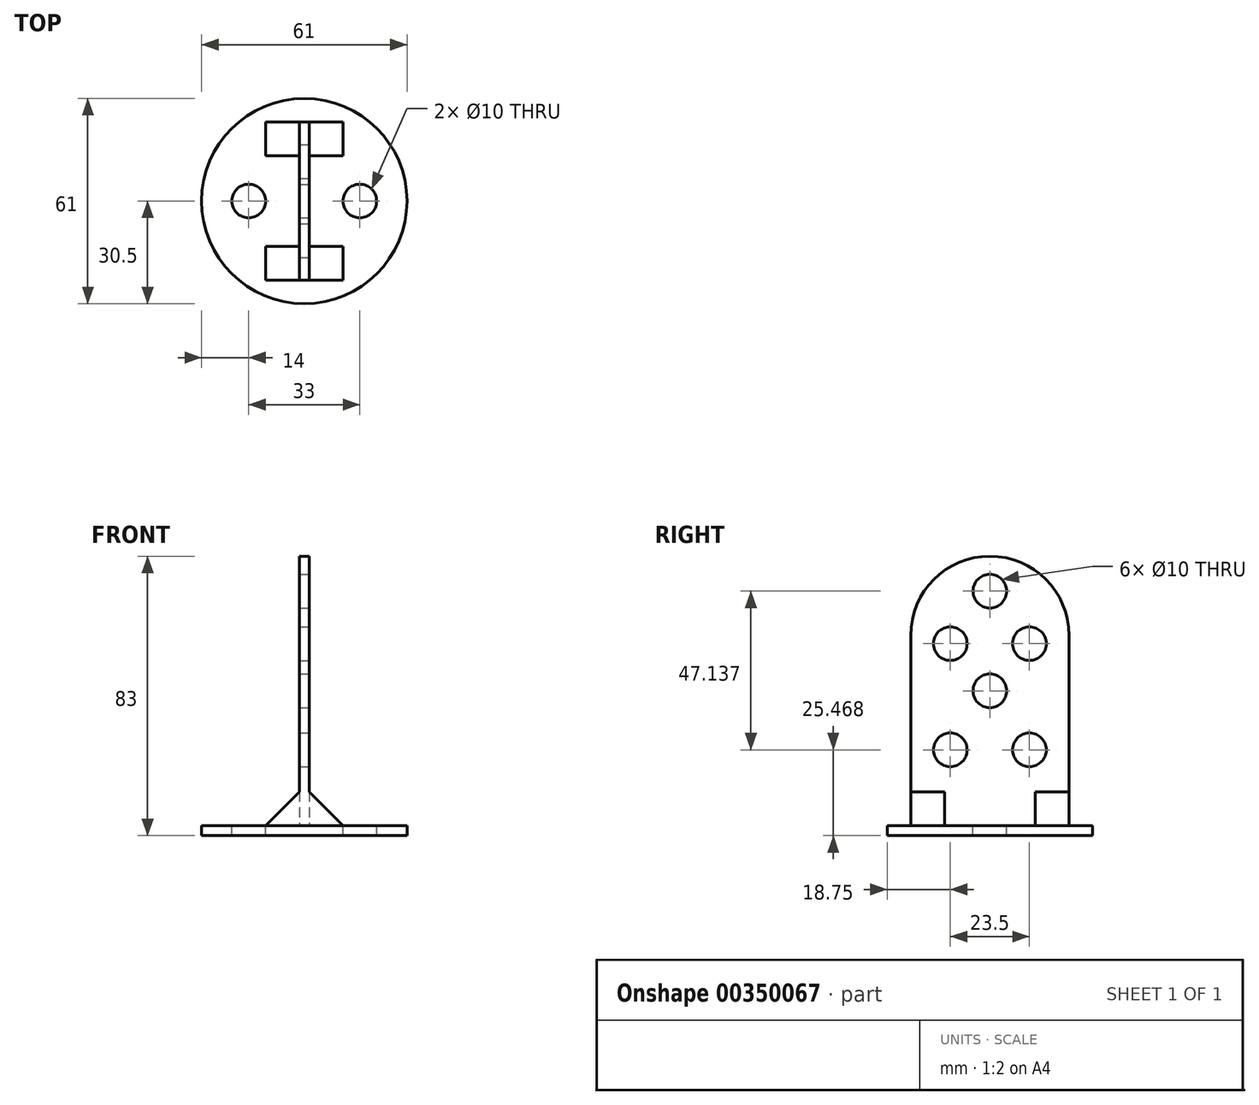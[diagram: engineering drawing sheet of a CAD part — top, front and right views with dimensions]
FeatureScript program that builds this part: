
annotation { "Feature Type Name" : "Feature", "Feature Type Description" : "" }
export const myFeature = defineFeature(function(context is Context, id is Id, definition is map)
    precondition{}
    {
        {
            var Q0;
            Q0=qCreatedBy(makeId("Top.planeOp"),FACE);
            var sketch = newSketch(context, id + "F0", { "sketchPlane" : qUnion([Q0])});
            skCircle(sketch, "E0", {"center": v(0, 0) * mm, "radius": 30.5 * mm});
            skSolve(sketch);
        }
        {
            var Q0;
            Q0=makeQuery(id+"F0.imprint","IMPRINT",FACE,{"disambiguationData":[TD([[makeQuery(id+"F0.imprint","IMPRINT",EDGE,{"derivedFrom":sQuery(id+"F0.wireOp",EDGE,"E0")}),1.0]])]});
            extrude(context, id + "F1", {"entities" : qUnion([Q0]), "depth" : 3 * mm});
        }
        {
            var Q0;
            Q0=makeQuery(id+"F1.opExtrude","CAP_FACE",FACE,{"disambiguationData":[OSD([sQuery(id+"F0.wireOp",EDGE,"E0")])],"isStart":false});
            var sketch = newSketch(context, id + "F2", { "sketchPlane" : qUnion([Q0])});
            skLineSegment(sketch, "E1", {"start": v(0, 56.72) * mm, "end": v(0, 23.5) * mm});
            skLineSegment(sketch, "E2", {"start": v(0, -59.64) * mm, "end": v(0, -23.5) * mm});
            skLineSegment(sketch, "E3", {"start": v(1.5, 0) * mm, "end": v(68.94, 0) * mm});
            skLineSegment(sketch, "E4", {"start": v(68.94, 0) * mm, "end": v(1.5, 0) * mm});
            skLineSegment(sketch, "E5.bottom", {"start": v(0, 23.5) * mm, "end": v(1.5, 23.5) * mm});
            skLineSegment(sketch, "E5.top", {"start": v(0, -23.5) * mm, "end": v(1.5, -23.5) * mm});
            skLineSegment(sketch, "E5.right", {"start": v(1.5, 23.5) * mm, "end": v(1.5, -23.5) * mm});
            skLineSegment(sketch, "E6.bottom", {"start": v(0, 23.5) * mm, "end": v(-1.5, 23.5) * mm});
            skLineSegment(sketch, "E6.top", {"start": v(0, -23.5) * mm, "end": v(-1.5, -23.5) * mm});
            skLineSegment(sketch, "E6.right", {"start": v(-1.5, 23.5) * mm, "end": v(-1.5, -23.5) * mm});
            skLineSegment(sketch, "E7.trimOffspring", {"start": v(0, -23.5) * mm, "end": v(0, -59.64) * mm});
            skLineSegment(sketch, "E8.trimOffspring", {"start": v(-1.5, 0) * mm, "end": v(-64.93, 0) * mm});
            skPoint(sketch, "E6.left.start.orphan", {"position": v(0, 0) * mm});
            skSolve(sketch);
        }
        {
            var Q0;
            {var subQ3=sQuery(id+"F2.wireOp",EDGE,"E5.bottom");Q0=makeQuery(id+"F2.imprint","IMPRINT",FACE,{"disambiguationData":[TD([[makeQuery(id+"F2.imprint","IMPRINT",EDGE,{"derivedFrom":subQ3}),-1.0]])]});}
            extrude(context, id + "F3", {"entities" : qUnion([Q0]), "operationType" : NewBodyOperationType.ADD, "depth" : 80 * mm});
        }
        {
            var Q0;
            Q0=makeQuery(id+"F3.opExtrude","CAP_EDGE",EDGE,{"disambiguationData":[OSD([sQuery(id+"F2.wireOp",EDGE,"E5.bottom"),sQuery(id+"F2.wireOp",EDGE,"E6.bottom")])],"isStart":false});
            var Q1;
            Q1=makeQuery(id+"F3.opExtrude","CAP_EDGE",EDGE,{"disambiguationData":[OSD([sQuery(id+"F2.wireOp",EDGE,"E5.top"),sQuery(id+"F2.wireOp",EDGE,"E6.top")])],"isStart":false});
            fillet(context, id + "F4", {"entities" : qUnion([Q0, Q1]), "radius" : 23.5 * mm, "tangentPropagation" : true, "allowEdgeOverflow" : false});
        }
        {
            var Q0;
            Q0=makeQuery(id+"F1.opExtrude","CAP_FACE",FACE,{"disambiguationData":[OSD([sQuery(id+"F0.wireOp",EDGE,"E0")])],"isStart":false});
            var sketch = newSketch(context, id + "F5", { "sketchPlane" : qUnion([Q0])});
            skLineSegment(sketch, "E9", {"start": v(1.5, -23.5) * mm, "end": v(1.5, -13.5) * mm});
            skLineSegment(sketch, "E10", {"start": v(1.5, -23.5) * mm, "end": v(11.5, -23.5) * mm});
            skLineSegment(sketch, "E11.top", {"start": v(1.5, -13.5) * mm, "end": v(11.5, -13.5) * mm});
            skLineSegment(sketch, "E11.right", {"start": v(11.5, -23.5) * mm, "end": v(11.5, -13.5) * mm});
            skSolve(sketch);
        }
        {
            var Q0;
            Q0=makeQuery(id+"F5.imprint","IMPRINT",FACE,{"disambiguationData":[TD([[makeQuery(id+"F5.imprint","IMPRINT",EDGE,{"derivedFrom":sQuery(id+"F5.wireOp",EDGE,"E10")}),1.0]])]});
            extrude(context, id + "F6", {"entities" : qUnion([Q0]), "operationType" : NewBodyOperationType.ADD, "depth" : 10 * mm});
        }
        {
            var Q0;
            Q0=makeQuery(id+"F6.opExtrude","CAP_EDGE",EDGE,{"disambiguationData":[OSD([sQuery(id+"F5.wireOp",EDGE,"E11.right")])],"isStart":false});
            chamfer(context, id + "F7", {"entities" : qUnion([Q0]), "width" : 10 * mm, "tangentPropagation" : true});
        }
        {
            var Q0;
            Q0=makeQuery(id+"F1.opExtrude","CAP_FACE",FACE,{"disambiguationData":[OSD([sQuery(id+"F0.wireOp",EDGE,"E0")])],"isStart":false});
            var sketch = newSketch(context, id + "F8", { "sketchPlane" : qUnion([Q0])});
            skLineSegment(sketch, "E12.bottom", {"start": v(1.5, 23.5) * mm, "end": v(11.5, 23.5) * mm});
            skLineSegment(sketch, "E12.top", {"start": v(1.5, 13.5) * mm, "end": v(11.5, 13.5) * mm});
            skLineSegment(sketch, "E12.left", {"start": v(1.5, 23.5) * mm, "end": v(1.5, 13.5) * mm});
            skLineSegment(sketch, "E12.right", {"start": v(11.5, 23.5) * mm, "end": v(11.5, 13.5) * mm});
            skLineSegment(sketch, "E13.bottom", {"start": v(-1.5, 23.5) * mm, "end": v(-11.5, 23.5) * mm});
            skLineSegment(sketch, "E13.top", {"start": v(-1.5, 13.5) * mm, "end": v(-11.5, 13.5) * mm});
            skLineSegment(sketch, "E13.left", {"start": v(-1.5, 23.5) * mm, "end": v(-1.5, 13.5) * mm});
            skLineSegment(sketch, "E13.right", {"start": v(-11.5, 23.5) * mm, "end": v(-11.5, 13.5) * mm});
            skLineSegment(sketch, "E14.bottom", {"start": v(-1.5, -23.5) * mm, "end": v(-11.5, -23.5) * mm});
            skLineSegment(sketch, "E14.top", {"start": v(-1.5, -13.5) * mm, "end": v(-11.5, -13.5) * mm});
            skLineSegment(sketch, "E14.left", {"start": v(-1.5, -23.5) * mm, "end": v(-1.5, -13.5) * mm});
            skLineSegment(sketch, "E14.right", {"start": v(-11.5, -23.5) * mm, "end": v(-11.5, -13.5) * mm});
            skSolve(sketch);
        }
        {
            var Q0;
            Q0=makeQuery(id+"F8.imprint","IMPRINT",FACE,{"disambiguationData":[TD([[makeQuery(id+"F8.imprint","IMPRINT",EDGE,{"derivedFrom":sQuery(id+"F8.wireOp",EDGE,"E12.bottom")}),-1.0]])]});
            var Q1;
            Q1=makeQuery(id+"F8.imprint","IMPRINT",FACE,{"disambiguationData":[TD([[makeQuery(id+"F8.imprint","IMPRINT",EDGE,{"derivedFrom":sQuery(id+"F8.wireOp",EDGE,"E13.bottom")}),1.0]])]});
            var Q2;
            Q2=makeQuery(id+"F8.imprint","IMPRINT",FACE,{"disambiguationData":[TD([[makeQuery(id+"F8.imprint","IMPRINT",EDGE,{"derivedFrom":sQuery(id+"F8.wireOp",EDGE,"E14.bottom")}),-1.0]])]});
            extrude(context, id + "F9", {"entities" : qUnion([Q0, Q1, Q2]), "operationType" : NewBodyOperationType.ADD, "depth" : 10 * mm});
        }
        {
            var Q0;
            Q0=makeQuery(id+"F9.opExtrude","CAP_EDGE",EDGE,{"disambiguationData":[OSD([sQuery(id+"F8.wireOp",EDGE,"E12.right")])],"isStart":false});
            var Q1;
            Q1=makeQuery(id+"F9.opExtrude","CAP_EDGE",EDGE,{"disambiguationData":[OSD([sQuery(id+"F8.wireOp",EDGE,"E13.right")])],"isStart":false});
            var Q2;
            Q2=makeQuery(id+"F9.opExtrude","CAP_EDGE",EDGE,{"disambiguationData":[OSD([sQuery(id+"F8.wireOp",EDGE,"E14.right")])],"isStart":false});
            chamfer(context, id + "F10", {"entities" : qUnion([Q0, Q1, Q2]), "width" : 10 * mm, "tangentPropagation" : true});
        }
        {
            var Q0;
            Q0=makeQuery(id+"F1.opExtrude","CAP_FACE",FACE,{"disambiguationData":[OSD([sQuery(id+"F0.wireOp",EDGE,"E0")])],"isStart":false});
            var sketch = newSketch(context, id + "F11", { "sketchPlane" : qUnion([Q0])});
            skLineSegment(sketch, "E15", {"start": v(1.5, -13.5) * mm, "end": v(1.5, 13.5) * mm});
            skLineSegment(sketch, "E16", {"start": v(1.5, 0) * mm, "end": v(16.5, 0) * mm});
            skPoint(sketch, "E16.endSnap0", {"position": v(1.5, 0) * mm});
            skLineSegment(sketch, "E17", {"start": v(1.5, 0) * mm, "end": v(-16.5, 0) * mm});
            skPoint(sketch, "E17.endSnap0", {"position": v(-1.5, 0) * mm});
            skCircle(sketch, "E18", {"center": v(-16.5, 0) * mm, "radius": 5 * mm});
            skCircle(sketch, "E19", {"center": v(16.5, 0) * mm, "radius": 5 * mm});
            skSolve(sketch);
        }
        {
            var Q0;
            Q0=makeQuery(id+"F11.imprint","IMPRINT",FACE,{"disambiguationData":[TD([[makeQuery(id+"F11.imprint","IMPRINT",EDGE,{"derivedFrom":sQuery(id+"F11.wireOp",EDGE,"E19")}),1.0]])]});
            var Q1;
            Q1=makeQuery(id+"F11.imprint","IMPRINT",FACE,{"disambiguationData":[TD([[makeQuery(id+"F11.imprint","IMPRINT",EDGE,{"derivedFrom":sQuery(id+"F11.wireOp",EDGE,"E18")}),1.0]])]});
            extrude(context, id + "F12", {"entities" : qUnion([Q0, Q1]), "operationType" : NewBodyOperationType.REMOVE, "oppositeDirection" : true, "depth" : 3 * mm});
        }
        {
            var Q0;
            Q0=makeQuery(id+"F3.opExtrude","SWEPT_FACE",FACE,{"disambiguationData":[OSD([sQuery(id+"F2.wireOp",EDGE,"E5.right")])]});
            var sketch = newSketch(context, id + "F13", { "sketchPlane" : qUnion([Q0])});
            skLineSegment(sketch, "E20", {"start": v(0, 3) * mm, "end": v(0, 38) * mm});
            skCircle(sketch, "E21", {"center": v(-11.75, 25.47) * mm, "radius": 5 * mm});
            skPoint(sketch, "E22.start.orphan", {"position": v(0, 25.47) * mm});
            skPoint(sketch, "E23.trimOffspring.end.orphan", {"position": v(-23.5, 25.47) * mm});
            skCircle(sketch, "E24", {"center": v(11.75, 25.47) * mm, "radius": 5 * mm});
            skPoint(sketch, "E25.start.orphan", {"position": v(0, 43) * mm});
            skPoint(sketch, "E26.end.orphan", {"position": v(23.5, 25.47) * mm});
            skCircle(sketch, "E27", {"center": v(-11.75, 57.02) * mm, "radius": 5 * mm});
            skCircle(sketch, "E28", {"center": v(11.75, 57.02) * mm, "radius": 5 * mm});
            skPoint(sketch, "E29.trimOffspring.end.orphan", {"position": v(-23.5, 57.02) * mm});
            skPoint(sketch, "E30.orphan", {"position": v(0, 57.02) * mm});
            skPoint(sketch, "E31.end.orphan", {"position": v(23.5, 57.02) * mm});
            skCircle(sketch, "E32", {"center": v(0, 43) * mm, "radius": 5 * mm});
            skCircle(sketch, "E33", {"center": v(0, 72.6) * mm, "radius": 5 * mm});
            skLineSegment(sketch, "E34.trimOffspring", {"start": v(0, 77.6) * mm, "end": v(0, 83) * mm});
            skLineSegment(sketch, "E35.trimOffspring", {"start": v(0, 48) * mm, "end": v(0, 67.6) * mm});
            skSolve(sketch);
        }
        {
            var Q0;
            {var subQ0=sQuery(id+"F13.wireOp",EDGE,"E33");var subQ1=makeQuery(id+"F13.imprint","INTERSECT",VERTEX,{"derivedFrom":[subQ0,sQuery(id+"F13.wireOp",EDGE,"E34.trimOffspring")]});Q0=makeQuery(id+"F13.imprint","IMPRINT",FACE,{"disambiguationData":[TD([[makeQuery(id+"F13.imprint","IMPRINT",EDGE,{"disambiguationData":[TD([[subQ1,-1.0]])],"derivedFrom":subQ0}),1.0]])]});}
            var Q1;
            Q1=makeQuery(id+"F13.imprint","IMPRINT",FACE,{"disambiguationData":[TD([[makeQuery(id+"F13.imprint","IMPRINT",EDGE,{"derivedFrom":sQuery(id+"F13.wireOp",EDGE,"E28")}),1.0]])]});
            var Q2;
            {var subQ0=sQuery(id+"F13.wireOp",EDGE,"E32");var subQ1=makeQuery(id+"F13.imprint","INTERSECT",VERTEX,{"derivedFrom":[sQuery(id+"F13.wireOp",EDGE,"E20"),subQ0]});Q2=makeQuery(id+"F13.imprint","IMPRINT",FACE,{"disambiguationData":[TD([[makeQuery(id+"F13.imprint","IMPRINT",EDGE,{"disambiguationData":[TD([[subQ1,1.0]])],"derivedFrom":subQ0}),1.0]])]});}
            var Q3;
            Q3=makeQuery(id+"F13.imprint","IMPRINT",FACE,{"disambiguationData":[TD([[makeQuery(id+"F13.imprint","IMPRINT",EDGE,{"derivedFrom":sQuery(id+"F13.wireOp",EDGE,"E27")}),1.0]])]});
            var Q4;
            Q4=makeQuery(id+"F13.imprint","IMPRINT",FACE,{"disambiguationData":[TD([[makeQuery(id+"F13.imprint","IMPRINT",EDGE,{"derivedFrom":sQuery(id+"F13.wireOp",EDGE,"E21")}),1.0]])]});
            var Q5;
            Q5=makeQuery(id+"F13.imprint","IMPRINT",FACE,{"disambiguationData":[TD([[makeQuery(id+"F13.imprint","IMPRINT",EDGE,{"derivedFrom":sQuery(id+"F13.wireOp",EDGE,"E24")}),1.0]])]});
            extrude(context, id + "F14", {"entities" : qUnion([Q0, Q1, Q2, Q3, Q4, Q5]), "operationType" : NewBodyOperationType.REMOVE, "oppositeDirection" : true, "depth" : 3 * mm});
        }
    });
